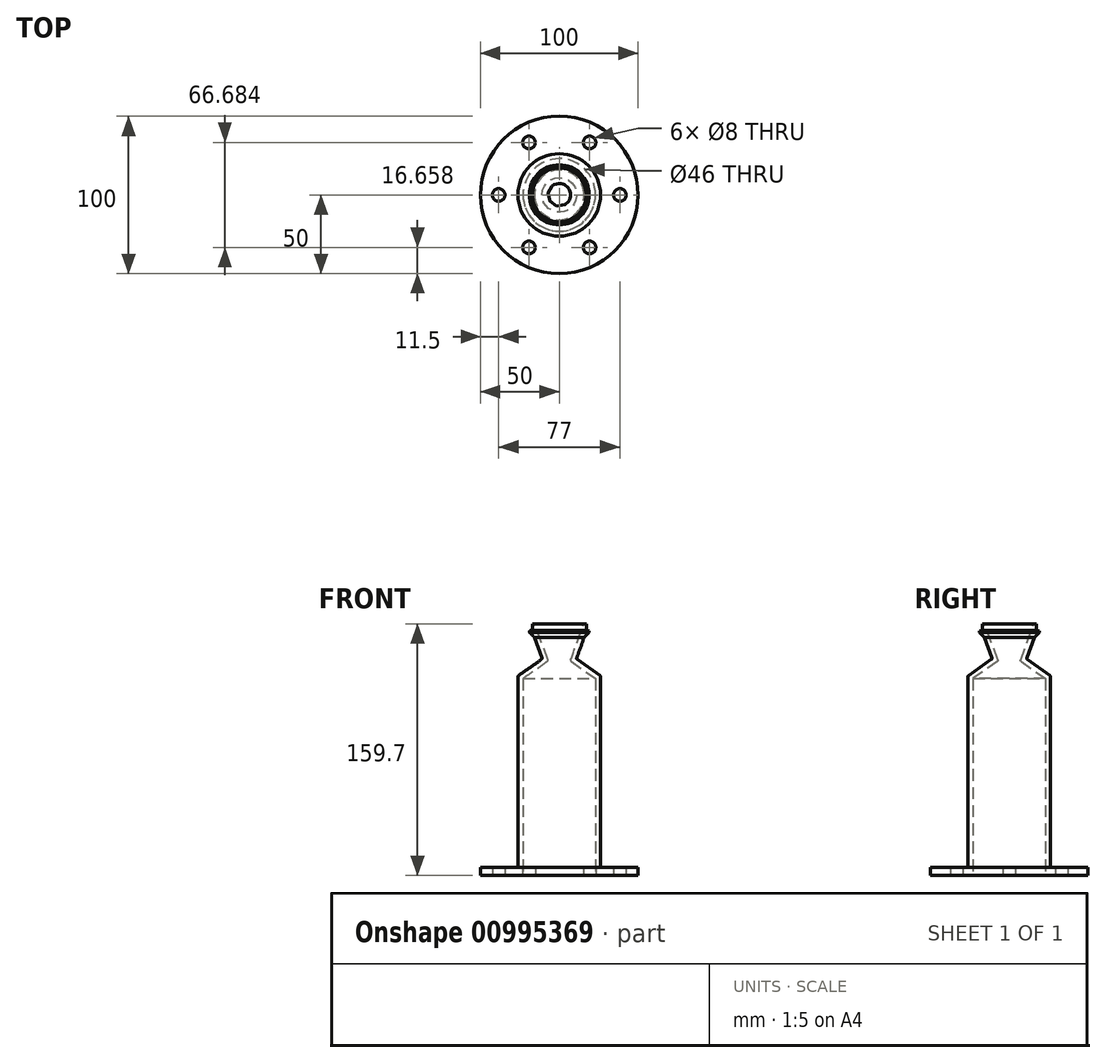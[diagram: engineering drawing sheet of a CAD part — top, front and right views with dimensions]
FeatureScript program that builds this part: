
annotation { "Feature Type Name" : "Feature", "Feature Type Description" : "" }
export const myFeature = defineFeature(function(context is Context, id is Id, definition is map)
    precondition{}
    {
        {
            var Q0;
            Q0=qCreatedBy(makeId("Top.planeOp"),FACE);
            var sketch = newSketch(context, id + "F0", { "sketchPlane" : qUnion([Q0])});
            skCircle(sketch, "E0", {"center": v(0, 0) * mm, "radius": 50 * mm});
            skCircle(sketch, "E1", {"center": v(0, 0) * mm, "radius": 23 * mm});
            skCircle(sketch, "E2", {"center": v(38.5, 0) * mm, "radius": 4 * mm});
            skCircle(sketch, "E3.1.0", {"center": v(19.25, 33.34) * mm, "radius": 4 * mm});
            skCircle(sketch, "E3.2.0", {"center": v(-19.25, 33.34) * mm, "radius": 4 * mm});
            skCircle(sketch, "E3.3.0", {"center": v(-38.5, 0) * mm, "radius": 4 * mm});
            skCircle(sketch, "E3.4.0", {"center": v(-19.25, -33.34) * mm, "radius": 4 * mm});
            skCircle(sketch, "E3.5.0", {"center": v(19.25, -33.34) * mm, "radius": 4 * mm});
            skSolve(sketch);
        }
        {
            var Q0;
            Q0=qCreatedBy(makeId("Front.planeOp"),FACE);
            var sketch = newSketch(context, id + "F1", { "sketchPlane" : qUnion([Q0])});
            skLineSegment(sketch, "E4", {"start": v(0, 0) * mm, "end": v(0, 160) * mm});
            skLineSegment(sketch, "E5", {"start": v(-23, 0) * mm, "end": v(-23, 125) * mm});
            skLineSegment(sketch, "E6", {"start": v(-23, 125) * mm, "end": v(-7, 136.2) * mm});
            skLineSegment(sketch, "E7", {"start": v(-7, 136.2) * mm, "end": v(-15.55, 159.7) * mm});
            skLineSegment(sketch, "E8.0", {"start": v(-10.85, 137.42) * mm, "end": v(-15.84, 151.14) * mm});
            skLineSegment(sketch, "E8.1", {"start": v(-26.2, 126.67) * mm, "end": v(-10.85, 137.42) * mm});
            skLineSegment(sketch, "E8.2", {"start": v(-26.2, 0) * mm, "end": v(-26.2, 126.67) * mm});
            skLineSegment(sketch, "E9", {"start": v(-15.84, 151.14) * mm, "end": v(-19.02, 154.29) * mm});
            skLineSegment(sketch, "E10", {"start": v(-19.02, 154.29) * mm, "end": v(-19.02, 155.26) * mm});
            skLineSegment(sketch, "E11", {"start": v(-19.02, 155.26) * mm, "end": v(-17.15, 155.7) * mm});
            skLineSegment(sketch, "E12", {"start": v(-17.15, 155.7) * mm, "end": v(-17.15, 159.7) * mm});
            skLineSegment(sketch, "E13", {"start": v(-17.15, 159.7) * mm, "end": v(-15.55, 159.7) * mm});
            skLineSegment(sketch, "E14", {"start": v(-26.2, 0) * mm, "end": v(-23, 0) * mm});
            skPoint(sketch, "E15", {"position": v(-17.15, 157.7) * mm});
            skPoint(sketch, "E16", {"position": v(-26.2, 5) * mm});
            skSolve(sketch);
        }
        {
            var Q0;
            Q0=makeQuery(id+"F0.imprint","IMPRINT",FACE,{"disambiguationData":[TD([[makeQuery(id+"F0.imprint","IMPRINT",EDGE,{"derivedFrom":sQuery(id+"F0.wireOp",EDGE,"E0")}),1.0]])]});
            extrude(context, id + "F2", {"entities" : qUnion([Q0]), "depth" : 5 * mm, "offsetDistance" : 25 * mm});
        }
        {
            var Q0;
            Q0=makeQuery(id+"F1.imprint","IMPRINT",FACE,{"disambiguationData":[TD([[makeQuery(id+"F1.imprint","IMPRINT",EDGE,{"derivedFrom":sQuery(id+"F1.wireOp",EDGE,"E5")}),1.0]])]});
            var Q1;
            Q1=sQuery(id+"F1.wireOp",EDGE,"E5");
            var Q2;
            Q2=sQuery(id+"F1.wireOp",EDGE,"E7");
            var Q3;
            Q3=sQuery(id+"F1.wireOp",EDGE,"E8.1");
            var Q4;
            Q4=sQuery(id+"F1.wireOp",EDGE,"E6");
            var Q5;
            Q5=sQuery(id+"F1.wireOp",EDGE,"E8.2");
            var Q6;
            Q6=sQuery(id+"F1.wireOp",EDGE,"E8.0");
            var Q7;
            Q7=sQuery(id+"F1.wireOp",EDGE,"E11");
            var Q8;
            Q8=sQuery(id+"F1.wireOp",EDGE,"E13");
            var Q9;
            Q9=sQuery(id+"F1.wireOp",EDGE,"E9");
            var Q10;
            Q10=sQuery(id+"F1.wireOp",EDGE,"E10");
            var Q11;
            Q11=sQuery(id+"F1.wireOp",EDGE,"E12");
            var Q12;
            Q12=sQuery(id+"F1.wireOp",EDGE,"E14");
            var Q13;
            Q13=sQuery(id+"F1.wireOp",EDGE,"E4");
            revolve(context, id + "F3", {"operationType" : NewBodyOperationType.ADD, "surfaceOperationType" : NewSurfaceOperationType.ADD, "entities" : qUnion([Q0]), "surfaceEntities" : qUnion([Q1, Q2, Q3, Q4, Q5, Q6, Q7, Q8, Q9, Q10, Q11, Q12]), "axis" : qUnion([Q13]), "revolveType" : RevolveType.FULL});
        }
        {
            var Q0;
            Q0=makeQuery(id+"F3.opRevolve","SWEPT_EDGE",EDGE,{"disambiguationData":[OSD([sQuery(id+"F1.wireOp",EDGE,"E6"),sQuery(id+"F1.wireOp",EDGE,"E7")])]});
            var Q1;
            Q1=makeQuery(id+"F3.opRevolve","SWEPT_EDGE",EDGE,{"disambiguationData":[OSD([sQuery(id+"F1.wireOp",EDGE,"E8.1"),sQuery(id+"F1.wireOp",EDGE,"E8.2")])]});
            var Q2;
            Q2=makeQuery(id+"F3.opRevolve","SWEPT_EDGE",EDGE,{"disambiguationData":[OSD([sQuery(id+"F1.wireOp",EDGE,"E7"),sQuery(id+"F1.wireOp",EDGE,"E13")])]});
            fillet(context, id + "F4", {"entities" : qUnion([Q0, Q1, Q2]), "radius" : 1 * mm, "tangentPropagation" : true, "allowEdgeOverflow" : false});
        }
        {
            var Q0;
            Q0=makeQuery(id+"F3.opRevolve","SWEPT_EDGE",EDGE,{"disambiguationData":[OSD([sQuery(id+"F1.wireOp",EDGE,"E8.0"),sQuery(id+"F1.wireOp",EDGE,"E8.1")])]});
            fillet(context, id + "F5", {"entities" : qUnion([Q0]), "radius" : 1 * mm, "tangentPropagation" : true, "allowEdgeOverflow" : false});
        }
    });
